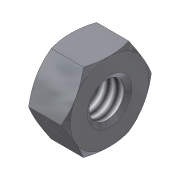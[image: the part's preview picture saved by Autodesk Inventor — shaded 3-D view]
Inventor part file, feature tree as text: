
AUTODESK INVENTOR PART (.ipt)
format: ipt  version: 2011 (Build 150239000, 239)  size: 136,192 bytes
history: native  units: mm (DEFAULTED — no unit token found)
features: chamfer x1, hole x1
ambient origin geometry x8: Origin, YZ Plane, XZ Plane, XY Plane, X Axis, Y Axis, Z Axis, Center Point
bodies: Solid1 (feature_tree), Body (feature_tree)
feature tree (2):
  chamfer  "Chamfer1"  Distance=12.83161mm
  hole  "Thread"  [1 undecoded]
note: 1 required parameter value undecoded (feature->parameter linkage not recoverable at this tier; creation-order binding heuristic only, values carry confidence <= 0.55)
